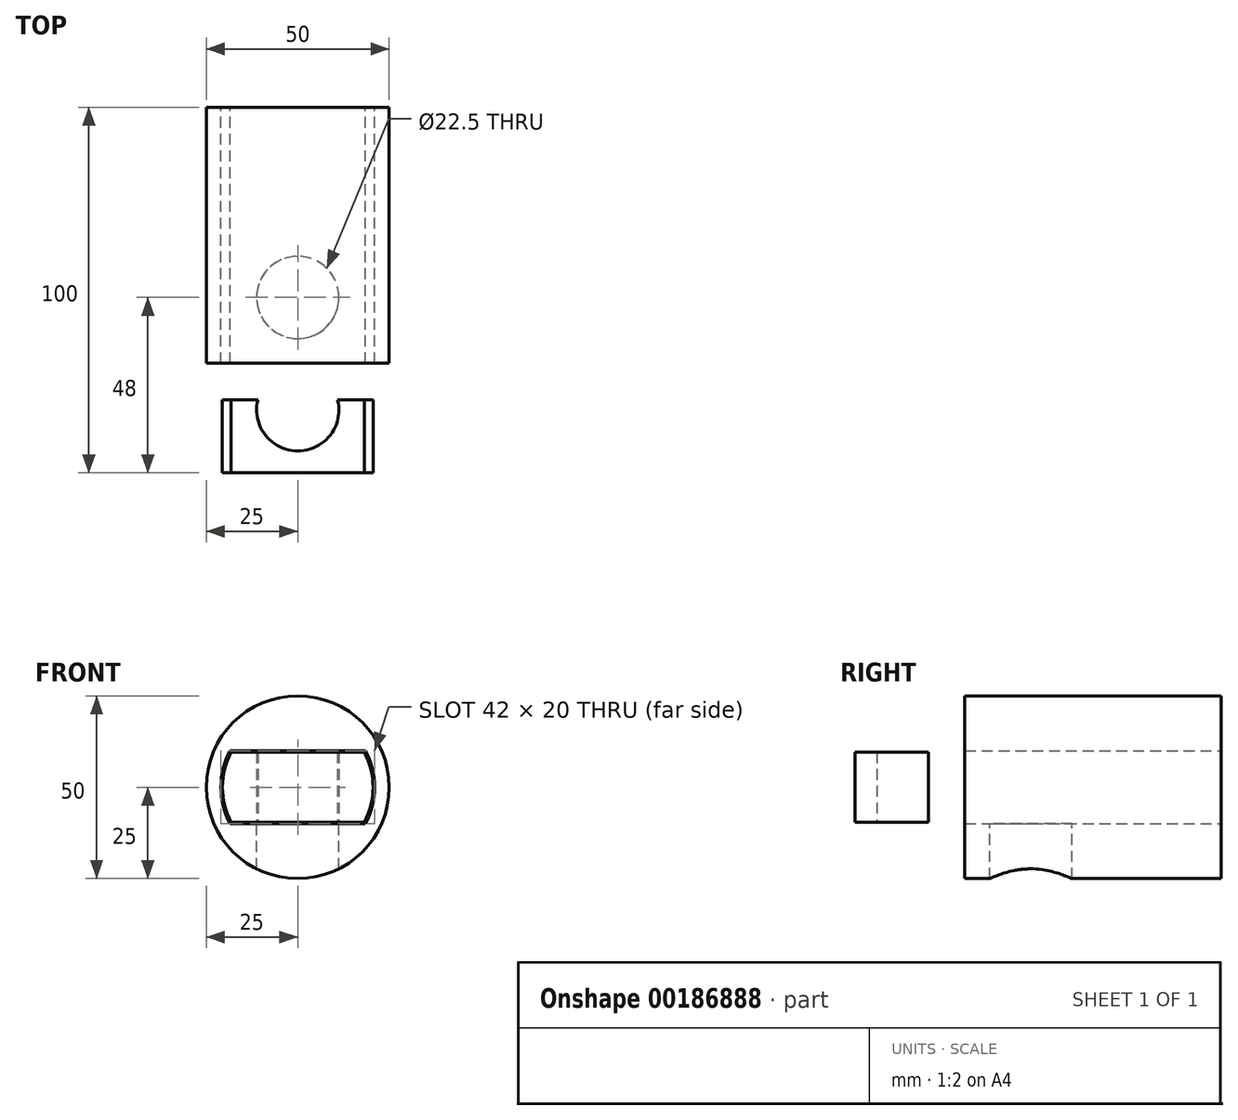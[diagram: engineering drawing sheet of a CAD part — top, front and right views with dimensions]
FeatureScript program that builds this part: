
annotation { "Feature Type Name" : "Feature", "Feature Type Description" : "" }
export const myFeature = defineFeature(function(context is Context, id is Id, definition is map)
    precondition{}
    {
        {
            var Q0;
            Q0=qCreatedBy(makeId("Front.planeOp"),FACE);
            var sketch = newSketch(context, id + "F0", { "sketchPlane" : qUnion([Q0])});
            skArc(sketch, "E0", {"start": v(-18.47, 10) * mm, "mid": v(-21, 0) * mm, "end": v(-18.47, -10) * mm});
            skLineSegment(sketch, "E1", {"start": v(-18.47, 10) * mm, "end": v(18.47, 10) * mm});
            skLineSegment(sketch, "E2", {"start": v(-18.47, -10) * mm, "end": v(18.47, -10) * mm});
            skCircle(sketch, "E3", {"center": v(0, 0) * mm, "radius": 25 * mm});
            skArc(sketch, "E4.trimOffspring", {"start": v(18.47, -10) * mm, "mid": v(21, 0) * mm, "end": v(18.47, 10) * mm});
            skSolve(sketch);
        }
        {
            var Q0;
            Q0 = qSketchRegion(id + "F0", true);
            extrude(context, id + "F1", {"entities" : qUnion([Q0]), "depth" : 70 * mm});
        }
        {
            var Q0;
            Q0=qCreatedBy(makeId("Top.planeOp"),FACE);
            var sketch = newSketch(context, id + "F2", { "sketchPlane" : qUnion([Q0])});
            skCircle(sketch, "E5", {"center": v(0, -52) * mm, "radius": 11.25 * mm});
            skSolve(sketch);
        }
        {
            var Q0;
            Q0 = qSketchRegion(id + "F2", true);
            extrude(context, id + "F3", {"entities" : qUnion([Q0]), "operationType" : NewBodyOperationType.REMOVE, "oppositeDirection" : true, "depth" : 25 * mm});
        }
        {
            var Q0;
            Q0=makeQuery(id+"F1.opExtrude","CAP_FACE",FACE,{"disambiguationData":[OSD([sQuery(id+"F0.wireOp",EDGE,"E0"),sQuery(id+"F0.wireOp",EDGE,"E1"),sQuery(id+"F0.wireOp",EDGE,"E2"),sQuery(id+"F0.wireOp",EDGE,"E3"),sQuery(id+"F0.wireOp",EDGE,"E4.trimOffspring")])],"isStart":false});
            cPlane(context, id + "F4", {"entities" : qUnion([Q0]), "cplaneType" : CPlaneType.OFFSET, "offset" : 10 * mm, "width" : 150 * mm, "height" : 150 * mm});
        }
        {
            var Q0;
            Q0=qCreatedBy(id+"F4.planeOp",FACE);
            var sketch = newSketch(context, id + "F5", { "sketchPlane" : qUnion([Q0])});
            skLineSegment(sketch, "E6.0", {"start": v(-18.23, 9.6) * mm, "end": v(18.23, 9.6) * mm});
            skArc(sketch, "E6.1", {"start": v(-18.23, 9.6) * mm, "mid": v(-20.6, 0) * mm, "end": v(-18.23, -9.6) * mm});
            skLineSegment(sketch, "E6.2", {"start": v(-18.23, -9.6) * mm, "end": v(18.23, -9.6) * mm});
            skArc(sketch, "E6.3", {"start": v(18.23, -9.6) * mm, "mid": v(20.6, 0) * mm, "end": v(18.23, 9.6) * mm});
            skSolve(sketch);
        }
        {
            var Q0;
            Q0=makeQuery(id+"F5.imprint","IMPRINT",FACE,{"disambiguationData":[TD([[makeQuery(id+"F5.imprint","IMPRINT",EDGE,{"derivedFrom":sQuery(id+"F5.wireOp",EDGE,"E6.0")}),-1.0]])]});
            extrude(context, id + "F6", {"entities" : qUnion([Q0]), "depth" : 20 * mm});
        }
        {
            var Q0;
            Q0=makeQuery(id+"F6.opExtrude","SWEPT_FACE",FACE,{"disambiguationData":[OSD([sQuery(id+"F5.wireOp",EDGE,"E6.2")])]});
            var sketch = newSketch(context, id + "F7", { "sketchPlane" : qUnion([Q0])});
            skCircle(sketch, "E7", {"center": v(0, 82.75) * mm, "radius": 11.25 * mm});
            skPoint(sketch, "E7.centerSnap0", {"position": v(0, 80) * mm});
            skSolve(sketch);
        }
        {
            var Q0;
            Q0 = qSketchRegion(id + "F7", true);
            extrude(context, id + "F8", {"entities" : qUnion([Q0]), "operationType" : NewBodyOperationType.REMOVE, "endBound" : BoundingType.UP_TO_NEXT, "oppositeDirection" : true, "depth" : 25 * mm});
        }
    });
